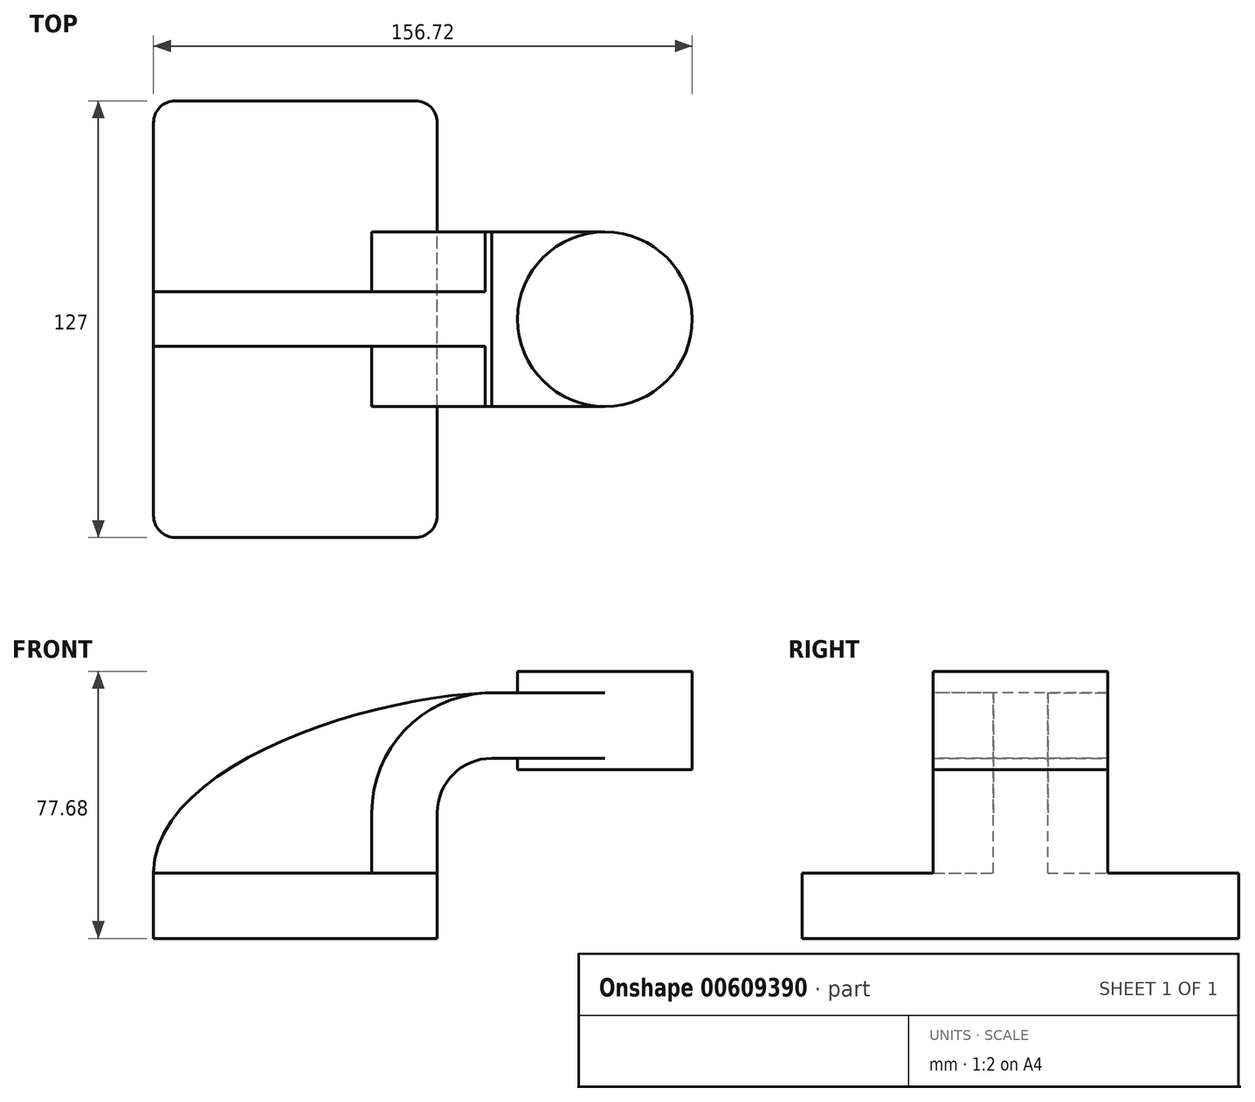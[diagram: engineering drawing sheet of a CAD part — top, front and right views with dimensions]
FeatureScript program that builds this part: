
annotation { "Feature Type Name" : "Feature", "Feature Type Description" : "" }
export const myFeature = defineFeature(function(context is Context, id is Id, definition is map)
    precondition{}
    {
        {
            var Q0;
            Q0=qCreatedBy(makeId("Front.planeOp"),FACE);
            var sketch = newSketch(context, id + "F0", { "sketchPlane" : qUnion([Q0])});
            skLineSegment(sketch, "E0.bottom", {"start": v(-41.28, -9.53) * mm, "end": v(41.28, -9.53) * mm});
            skLineSegment(sketch, "E0.top", {"start": v(-41.28, 9.53) * mm, "end": v(41.28, 9.53) * mm});
            skLineSegment(sketch, "E0.left", {"start": v(-41.28, -9.53) * mm, "end": v(-41.28, 9.53) * mm});
            skLineSegment(sketch, "E0.right", {"start": v(41.28, -9.53) * mm, "end": v(41.28, 9.53) * mm});
            skPoint(sketch, "E0.middle", {"position": v(0, 0) * mm});
            skLineSegment(sketch, "E1", {"start": v(41.27, 9.52) * mm, "end": v(41.27, 27) * mm});
            skArc(sketch, "E2", {"start": v(41.27, 27) * mm, "mid": v(45.92, 38.23) * mm, "end": v(57.15, 42.88) * mm});
            skLineSegment(sketch, "E3", {"start": v(57.15, 42.88) * mm, "end": v(90.04, 42.88) * mm});
            skArc(sketch, "E4.0", {"start": v(22.22, 27) * mm, "mid": v(32.45, 51.7) * mm, "end": v(57.15, 61.93) * mm});
            skLineSegment(sketch, "E5.0", {"start": v(22.22, 9.52) * mm, "end": v(22.22, 27) * mm});
            skLineSegment(sketch, "E6.0", {"start": v(57.15, 61.93) * mm, "end": v(90.04, 61.93) * mm});
            skFitSpline(sketch, "E7", {"points": [v(-41.28, 9.53) * mm, v(57.15, 61.93) * mm], "startDerivative": vector(0.5, 94.52) * mm, "endDerivative": vector(106, 1.96) * mm});
            skLineSegment(sketch, "E8.bottom", {"start": v(90.04, 39.57) * mm, "end": v(115.44, 39.57) * mm});
            skLineSegment(sketch, "E8.top", {"start": v(90.04, 68.15) * mm, "end": v(115.44, 68.15) * mm});
            skLineSegment(sketch, "E8.right", {"start": v(115.44, 39.57) * mm, "end": v(115.44, 68.15) * mm});
            skLineSegment(sketch, "E9", {"start": v(90.04, 68.15) * mm, "end": v(90.04, 39.57) * mm});
            skSolve(sketch);
        }
        {
            var Q0;
            Q0=makeQuery(id+"F0.imprint","IMPRINT",FACE,{"disambiguationData":[TD([[makeQuery(id+"F0.imprint","IMPRINT",EDGE,{"derivedFrom":sQuery(id+"F0.wireOp",EDGE,"E0.bottom")}),1.0]])]});
            extrude(context, id + "F1", {"entities" : qUnion([Q0]), "endBound" : BoundingType.SYMMETRIC, "depth" : 127 * mm, "offsetDistance" : 25.4 * mm});
        }
        {
            var Q0;
            {var subQ3=sQuery(id+"F0.wireOp",EDGE,"E5.0");Q0=makeQuery(id+"F0.imprint","IMPRINT",FACE,{"disambiguationData":[TD([[makeQuery(id+"F0.imprint","IMPRINT",EDGE,{"derivedFrom":subQ3}),1.0]])]});}
            extrude(context, id + "F2", {"entities" : qUnion([Q0]), "operationType" : NewBodyOperationType.ADD, "endBound" : BoundingType.SYMMETRIC, "depth" : 15.88 * mm, "offsetDistance" : 25.4 * mm});
        }
        {
            var Q0;
            {var subQ1=sQuery(id+"F0.wireOp",EDGE,"E1");Q0=makeQuery(id+"F0.imprint","IMPRINT",FACE,{"disambiguationData":[TD([[makeQuery(id+"F0.imprint","IMPRINT",EDGE,{"derivedFrom":subQ1}),1.0]])]});}
            var Q1;
            {var subQ0=sQuery(id+"F0.wireOp",EDGE,"E3");var subQ1=sQuery(id+"F0.wireOp",EDGE,"74dOTd4b-AE5Z-dE6W-NbRU-duh9UKHq4QWD.left");var subQ2=makeQuery(id+"F0.imprint","INTERSECT",VERTEX,{"derivedFrom":[subQ1,subQ0]});Q1=makeQuery(id+"F0.imprint","IMPRINT",FACE,{"disambiguationData":[TD([[makeQuery(id+"F0.imprint","IMPRINT",EDGE,{"disambiguationData":[TD([[subQ2,-1.0]])],"derivedFrom":subQ1}),-1.0]])]});}
            extrude(context, id + "F3", {"entities" : qUnion([Q0, Q1]), "operationType" : NewBodyOperationType.ADD, "endBound" : BoundingType.SYMMETRIC, "depth" : 50.8 * mm, "offsetDistance" : 25.4 * mm});
        }
        {
            var Q0;
            {var subQ3=sQuery(id+"F0.wireOp",EDGE,"E8.bottom");Q0=makeQuery(id+"F0.imprint","IMPRINT",FACE,{"disambiguationData":[TD([[makeQuery(id+"F0.imprint","IMPRINT",EDGE,{"derivedFrom":subQ3}),1.0]])]});}
            var Q1;
            Q1=sQuery(id+"F0.wireOp",EDGE,"E9");
            revolve(context, id + "F4", {"operationType" : NewBodyOperationType.ADD, "entities" : qUnion([Q0]), "axis" : qUnion([Q1]), "revolveType" : RevolveType.FULL});
        }
        {
            var Q0;
            Q0=makeQuery(id+"F1.opExtrude","CAP_EDGE",EDGE,{"disambiguationData":[OSD([sQuery(id+"F0.wireOp",EDGE,"E0.left")])],"isStart":false});
            var Q1;
            Q1=makeQuery(id+"F1.opExtrude","CAP_EDGE",EDGE,{"disambiguationData":[OSD([sQuery(id+"F0.wireOp",EDGE,"E0.right")])],"isStart":false});
            var Q2;
            Q2=makeQuery(id+"F1.opExtrude","CAP_EDGE",EDGE,{"disambiguationData":[OSD([sQuery(id+"F0.wireOp",EDGE,"E0.right")])],"isStart":true});
            var Q3;
            Q3=makeQuery(id+"F1.opExtrude","CAP_EDGE",EDGE,{"disambiguationData":[OSD([sQuery(id+"F0.wireOp",EDGE,"E0.left")])],"isStart":true});
            fillet(context, id + "F5", {"entities" : qUnion([Q0, Q1, Q2, Q3]), "radius" : 6.35 * mm, "tangentPropagation" : true, "allowEdgeOverflow" : false});
        }
    });
